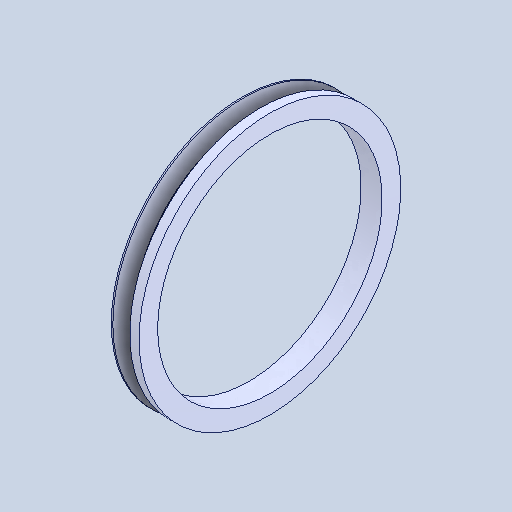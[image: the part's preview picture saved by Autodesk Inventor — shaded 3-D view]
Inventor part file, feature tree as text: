
AUTODESK INVENTOR PART (.ipt)
format: ipt  version: 2024.1 (Build 281209000, 209)  size: 129,024 bytes
history: native  units: in
note: dims shown in document units (in); Inventor stores cm internally (conversion verified against a paired STEP export)
features: revolve x1
ambient origin geometry x8: Origin, YZ Plane, XZ Plane, XY Plane, X Axis, Y Axis, Z Axis, Center Point
bodies: Solid1 (feature_tree)
feature tree (1):
  revolve  "Revolve1"  [1 undecoded]
note: 1 required parameter value undecoded (feature->parameter linkage not recoverable at this tier; creation-order binding heuristic only, values carry confidence <= 0.55)
